# Revit family: Faucet-Lavatory-American_Standard-Townsend-7353.801_Series
name_source: partatom
category: Plumbing Fixtures
units: mm (PartAtom-declared; Revit-internal decimal feet)

## family parameters
Always vertical = No
Cut with Voids When Loaded = No
OmniClass Number = 23.45.55.17
OmniClass Title = Mixing Faucets
Part Type = Normal
Room Calculation Point = No
Round Connector Dimension = Use Diameter
Shared = Yes
Work Plane-Based = Yes

## types (4) — shared parameters
ADA Compliant = Yes
Assembly Code = D2020300
CW Connection = Yes
CWFU = 1.5
Cold Water Connection Diameter = 3/8"
Cold Water Connection Radius = 3/16"
Default Elevation = 0"
Description = Townsend Two-Handle Widespread Lavatory Faucet
Flow Rate = 1.2 gpm (4.5 L/min.)
HW Connection = Yes
HWFU = 1.5
Height = 7 15/16"
Hot Water Connection Diameter = 3/8"
Hot Water Connection Radius = 3/16"
Length = 6 3/4"
Manufacturer = American Standard
Product Documentation Link = https://www.americanstandard-us.com
Product Page URL = https://www.americanstandard-us.com
Revised Date = 04/14/2021
URL = https://www.americanstandard-us.com
Vent Connection = No
WFU = 2
Waste Connection = No
Width = 14 1/16"

## per-type parameters (varying)
| type | Finish | Material |
| 7353.801.002 | Brass-American Standard-002-Polished Chrome | Brass-American Standard-002-Polished Chrome |
| 7353.801.013 | Brass-American Standard-013-Polished Nickel | Brass-American Standard-013-Polished Nickel |
| 7353.801.278 | Brass-American Standard-278-Legacy Bronze | Brass-American Standard-278-Legacy Bronze |
| 7353.801.295 | Brass-American Standard-295-Brushed Nickel | Brass-American Standard-295-Brushed Nickel |

note: column(s) folded — value = type name in every type: Model

## geometry (parser evidence)
native form markers: Sweep x2
no freeform markers — native parametric forms only
